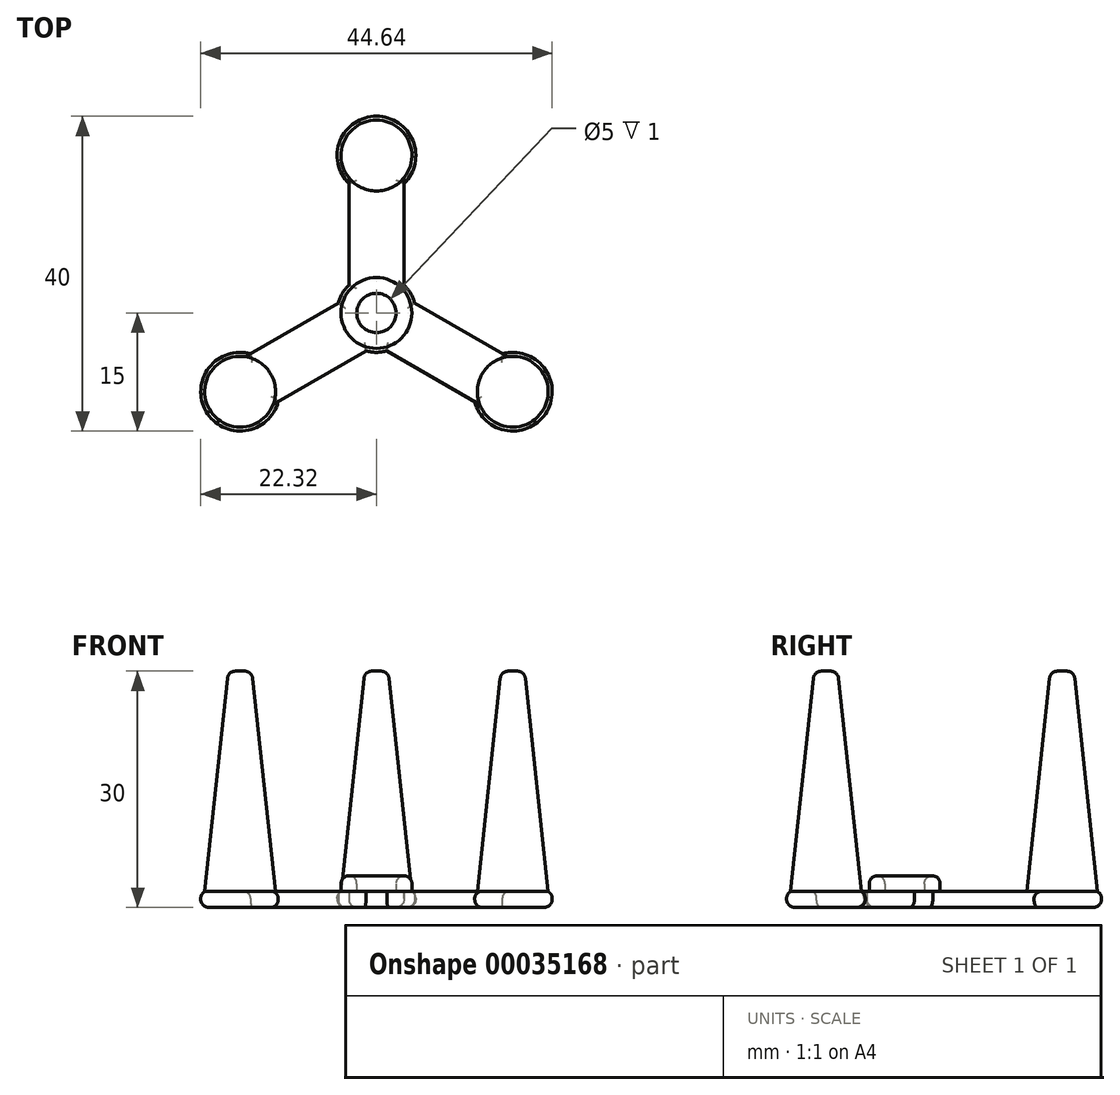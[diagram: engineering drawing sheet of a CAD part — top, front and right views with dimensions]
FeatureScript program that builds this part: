
annotation { "Feature Type Name" : "Feature", "Feature Type Description" : "" }
export const myFeature = defineFeature(function(context is Context, id is Id, definition is map)
    precondition{}
    {
        {
            var Q0;
            Q0=qCreatedBy(makeId("Top.planeOp"),FACE);
            var sketch = newSketch(context, id + "F0", { "sketchPlane" : qUnion([Q0])});
            skLineSegment(sketch, "E0", {"start": v(0, 0) * mm, "end": v(0, 20) * mm, "construction": true});
            skPoint(sketch, "E1.center", {"position": v(0, 0) * mm});
            skCircle(sketch, "E2", {"center": v(0, 20) * mm, "radius": 5 * mm});
            skCircle(sketch, "E3", {"center": v(0, 0) * mm, "radius": 5 * mm});
            skLineSegment(sketch, "E4", {"start": v(-3.5, 16.43) * mm, "end": v(3.5, 16.43) * mm, "construction": true});
            skLineSegment(sketch, "E5", {"start": v(-3.5, 16.43) * mm, "end": v(-3.5, 3.57) * mm});
            skLineSegment(sketch, "E6", {"start": v(3.5, 16.43) * mm, "end": v(3.5, 3.57) * mm});
            skCircle(sketch, "E7.1.0", {"center": v(-17.32, -10) * mm, "radius": 5 * mm});
            skLineSegment(sketch, "E7.1.1", {"start": v(-12.48, -11.25) * mm, "end": v(-1.34, -4.82) * mm});
            skLineSegment(sketch, "E7.1.2", {"start": v(-15.98, -5.18) * mm, "end": v(-4.84, 1.25) * mm});
            skCircle(sketch, "E7.2.0", {"center": v(17.32, -10) * mm, "radius": 5 * mm});
            skLineSegment(sketch, "E7.2.1", {"start": v(15.98, -5.18) * mm, "end": v(4.84, 1.25) * mm});
            skLineSegment(sketch, "E7.2.2", {"start": v(12.48, -11.25) * mm, "end": v(1.34, -4.82) * mm});
            skSolve(sketch);
        }
        {
            var Q0;
            Q0 = qSketchRegion(id + "F0", true);
            extrude(context, id + "F1", {"entities" : qUnion([Q0]), "depth" : 2 * mm});
        }
        {
            var Q0;
            Q0=qCreatedBy(makeId("Top.planeOp"),FACE);
            cPlane(context, id + "F2", {"entities" : qUnion([Q0]), "cplaneType" : CPlaneType.OFFSET, "offset" : 30 * mm, "width" : 150 * mm, "height" : 150 * mm});
        }
        {
            var Q0;
            Q0=qCreatedBy(id+"F2.planeOp",FACE);
            var sketch = newSketch(context, id + "F3", { "sketchPlane" : qUnion([Q0])});
            skPoint(sketch, "E8.0", {"position": v(0, 20) * mm});
            skPoint(sketch, "E9.0", {"position": v(-17.32, -10) * mm});
            skPoint(sketch, "E10.0", {"position": v(17.32, -10) * mm});
            skCircle(sketch, "E11", {"center": v(0, 20) * mm, "radius": 1.5 * mm});
            skCircle(sketch, "E12", {"center": v(-17.32, -10) * mm, "radius": 1.5 * mm});
            skCircle(sketch, "E13", {"center": v(17.32, -10) * mm, "radius": 1.5 * mm});
            skSolve(sketch);
        }
        {
            var Q0;
            Q0=makeQuery(id+"F1.opExtrude","CAP_FACE",FACE,{"disambiguationData":[OSD([sQuery(id+"F0.wireOp",EDGE,"E2"),sQuery(id+"F0.wireOp",EDGE,"E3"),sQuery(id+"F0.wireOp",EDGE,"E5"),sQuery(id+"F0.wireOp",EDGE,"E6"),sQuery(id+"F0.wireOp",EDGE,"E7.1.0"),sQuery(id+"F0.wireOp",EDGE,"E7.1.1"),sQuery(id+"F0.wireOp",EDGE,"E7.1.2"),sQuery(id+"F0.wireOp",EDGE,"E7.2.0"),sQuery(id+"F0.wireOp",EDGE,"E7.2.1"),sQuery(id+"F0.wireOp",EDGE,"E7.2.2")])],"isStart":false});
            var sketch = newSketch(context, id + "F4", { "sketchPlane" : qUnion([Q0])});
            skCircle(sketch, "E14", {"center": v(0, 20) * mm, "radius": 4.5 * mm});
            skCircle(sketch, "E15", {"center": v(-17.32, -10) * mm, "radius": 4.5 * mm});
            skCircle(sketch, "E16", {"center": v(17.32, -10) * mm, "radius": 4.5 * mm});
            skSolve(sketch);
        }
        {
            var Q1;
            Q1=makeQuery(id+"F4.imprint","IMPRINT",FACE,{"disambiguationData":[TD([[makeQuery(id+"F4.imprint","IMPRINT",EDGE,{"derivedFrom":sQuery(id+"F4.wireOp",EDGE,"E14")}),1.0]])]});
            var Q2;
            Q2=makeQuery(id+"F3.imprint","IMPRINT",FACE,{"disambiguationData":[TD([[makeQuery(id+"F3.imprint","IMPRINT",EDGE,{"derivedFrom":sQuery(id+"F3.wireOp",EDGE,"E11")}),1.0]])]});
            loft(context, id + "F5", {"operationType" : NewBodyOperationType.ADD, "sheetProfilesArray" : [{ "sheetProfileEntities" : qUnion([Q1]) }, { "sheetProfileEntities" : qUnion([Q2]) }]});
        }
        {
            var Q1;
            Q1=makeQuery(id+"F4.imprint","IMPRINT",FACE,{"disambiguationData":[TD([[makeQuery(id+"F4.imprint","IMPRINT",EDGE,{"derivedFrom":sQuery(id+"F4.wireOp",EDGE,"E15")}),1.0]])]});
            var Q2;
            Q2=makeQuery(id+"F3.imprint","IMPRINT",FACE,{"disambiguationData":[TD([[makeQuery(id+"F3.imprint","IMPRINT",EDGE,{"derivedFrom":sQuery(id+"F3.wireOp",EDGE,"E12")}),1.0]])]});
            loft(context, id + "F6", {"operationType" : NewBodyOperationType.ADD, "sheetProfilesArray" : [{ "sheetProfileEntities" : qUnion([Q1]) }, { "sheetProfileEntities" : qUnion([Q2]) }]});
        }
        {
            var Q1;
            Q1=makeQuery(id+"F4.imprint","IMPRINT",FACE,{"disambiguationData":[TD([[makeQuery(id+"F4.imprint","IMPRINT",EDGE,{"derivedFrom":sQuery(id+"F4.wireOp",EDGE,"E16")}),1.0]])]});
            var Q2;
            Q2=makeQuery(id+"F3.imprint","IMPRINT",FACE,{"disambiguationData":[TD([[makeQuery(id+"F3.imprint","IMPRINT",EDGE,{"derivedFrom":sQuery(id+"F3.wireOp",EDGE,"E13")}),1.0]])]});
            loft(context, id + "F7", {"operationType" : NewBodyOperationType.ADD, "sheetProfilesArray" : [{ "sheetProfileEntities" : qUnion([Q1]) }, { "sheetProfileEntities" : qUnion([Q2]) }]});
        }
        {
            var Q0;
            Q0=makeQuery(id+"F1.opExtrude","CAP_FACE",FACE,{"disambiguationData":[OSD([sQuery(id+"F0.wireOp",EDGE,"E2"),sQuery(id+"F0.wireOp",EDGE,"E3"),sQuery(id+"F0.wireOp",EDGE,"E5"),sQuery(id+"F0.wireOp",EDGE,"E6"),sQuery(id+"F0.wireOp",EDGE,"E7.1.0"),sQuery(id+"F0.wireOp",EDGE,"E7.1.1"),sQuery(id+"F0.wireOp",EDGE,"E7.1.2"),sQuery(id+"F0.wireOp",EDGE,"E7.2.0"),sQuery(id+"F0.wireOp",EDGE,"E7.2.1"),sQuery(id+"F0.wireOp",EDGE,"E7.2.2")])],"isStart":false});
            var sketch = newSketch(context, id + "F8", { "sketchPlane" : qUnion([Q0])});
            skCircle(sketch, "E17", {"center": v(0, 0) * mm, "radius": 4.5 * mm});
            skCircle(sketch, "E18", {"center": v(0, 0) * mm, "radius": 2.5 * mm});
            skSolve(sketch);
        }
        {
            var Q0;
            Q0 = qSketchRegion(id + "F8", true);
            extrude(context, id + "F9", {"entities" : qUnion([Q0]), "operationType" : NewBodyOperationType.ADD, "depth" : 2 * mm});
        }
        {
            var Q0;
            Q0=makeQuery(id+"F5.opLoft","CAP_FACE",FACE,{"disambiguationData":[OSD([makeQuery(id+"F3.imprint","IMPRINT",FACE,{"disambiguationData":[TD([[makeQuery(id+"F3.imprint","IMPRINT",EDGE,{"derivedFrom":sQuery(id+"F3.wireOp",EDGE,"E11")}),1.0]])]})])],"isStart":true});
            var Q1;
            Q1=makeQuery(id+"F6.opLoft","MID_CAP_EDGE",EDGE,{"disambiguationData":[OSD([sQuery(id+"F3.wireOp",EDGE,"E12"),sQuery(id+"F4.wireOp",EDGE,"E15")])],"capPos":1.0});
            var Q2;
            Q2=makeQuery(id+"F7.opLoft","MID_CAP_EDGE",EDGE,{"disambiguationData":[OSD([sQuery(id+"F3.wireOp",EDGE,"E13"),sQuery(id+"F4.wireOp",EDGE,"E16")])],"capPos":1.0});
            var Q3;
            Q3=makeQuery(id+"F1.opExtrude","CAP_FACE",FACE,{"disambiguationData":[OSD([sQuery(id+"F0.wireOp",EDGE,"E2"),sQuery(id+"F0.wireOp",EDGE,"E3"),sQuery(id+"F0.wireOp",EDGE,"E5"),sQuery(id+"F0.wireOp",EDGE,"E6"),sQuery(id+"F0.wireOp",EDGE,"E7.1.0"),sQuery(id+"F0.wireOp",EDGE,"E7.1.1"),sQuery(id+"F0.wireOp",EDGE,"E7.1.2"),sQuery(id+"F0.wireOp",EDGE,"E7.2.0"),sQuery(id+"F0.wireOp",EDGE,"E7.2.1"),sQuery(id+"F0.wireOp",EDGE,"E7.2.2")])],"isStart":true});
            var Q4;
            Q4=makeQuery(id+"F1.opExtrude","CAP_EDGE",EDGE,{"disambiguationData":[OSD([sQuery(id+"F0.wireOp",EDGE,"E7.1.0")])],"isStart":false});
            var Q5;
            Q5=makeQuery(id+"F1.opExtrude","CAP_EDGE",EDGE,{"disambiguationData":[OSD([sQuery(id+"F0.wireOp",EDGE,"E7.2.0")])],"isStart":false});
            var Q6;
            Q6=makeQuery(id+"F1.opExtrude","CAP_EDGE",EDGE,{"disambiguationData":[OSD([sQuery(id+"F0.wireOp",EDGE,"E2")])],"isStart":false});
            var Q7;
            Q7=makeQuery(id+"F9.opExtrude","CAP_FACE",FACE,{"disambiguationData":[OSD([sQuery(id+"F8.wireOp",EDGE,"E17"),sQuery(id+"F8.wireOp",EDGE,"E18")])],"isStart":false});
            fillet(context, id + "F10", {"entities" : qUnion([Q0, Q1, Q2, Q3, Q4, Q5, Q6, Q7]), "radius" : 1 * mm, "tangentPropagation" : true, "allowEdgeOverflow" : false});
        }
    });
